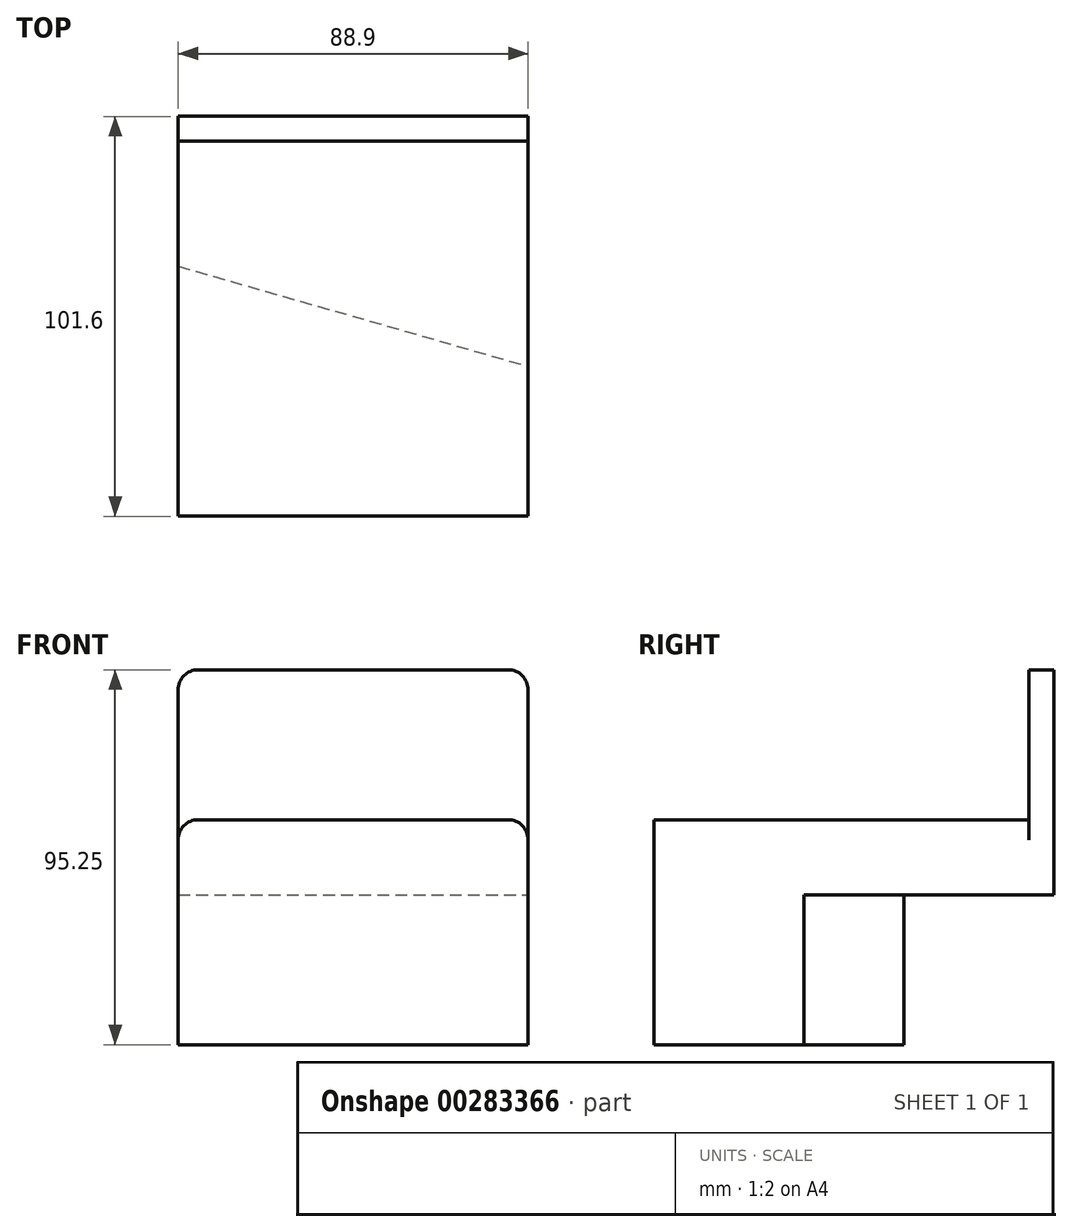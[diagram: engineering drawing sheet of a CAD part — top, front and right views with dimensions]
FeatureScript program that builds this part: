
annotation { "Feature Type Name" : "Feature", "Feature Type Description" : "" }
export const myFeature = defineFeature(function(context is Context, id is Id, definition is map)
    precondition{}
    {
        {
            var Q0;
            Q0=qCreatedBy(makeId("Top.planeOp"),FACE);
            var sketch = newSketch(context, id + "F0", { "sketchPlane" : qUnion([Q0])});
            skLineSegment(sketch, "E0", {"start": v(-31.98, -40.3) * mm, "end": v(56.92, -40.3) * mm});
            skLineSegment(sketch, "E1", {"start": v(56.92, -40.3) * mm, "end": v(56.92, -2.2) * mm});
            skLineSegment(sketch, "E2", {"start": v(-31.98, -40.3) * mm, "end": v(-31.98, 23.2) * mm});
            skLineSegment(sketch, "E3", {"start": v(-31.98, 23.2) * mm, "end": v(56.92, -2.2) * mm});
            skSolve(sketch);
        }
        {
            var Q0;
            Q0 = qSketchRegion(id + "F0", true);
            var Q1;
            Q1 = qSketchRegion(id + "F2", true);
            extrude(context, id + "F1", {"entities" : qUnion([Q0, Q1]), "depth" : 38.1 * mm});
        }
        {
            var Q0;
            Q0=makeQuery(id+"F1.opExtrude","CAP_FACE",FACE,{"disambiguationData":[OSD([sQuery(id+"F0.wireOp",EDGE,"E0"),sQuery(id+"F0.wireOp",EDGE,"E1"),sQuery(id+"F0.wireOp",EDGE,"E2"),sQuery(id+"F0.wireOp",EDGE,"E3")])],"isStart":false});
            var sketch = newSketch(context, id + "F2", { "sketchPlane" : qUnion([Q0])});
            skLineSegment(sketch, "E4.bottom", {"start": v(-31.98, -40.3) * mm, "end": v(56.92, -40.3) * mm});
            skLineSegment(sketch, "E4.top", {"start": v(-31.98, 61.3) * mm, "end": v(56.92, 61.3) * mm});
            skLineSegment(sketch, "E4.left", {"start": v(-31.98, -40.3) * mm, "end": v(-31.98, 61.3) * mm});
            skLineSegment(sketch, "E4.right", {"start": v(56.92, -40.3) * mm, "end": v(56.92, 61.3) * mm});
            skSolve(sketch);
        }
        {
            var Q0;
            Q0 = qSketchRegion(id + "F2", true);
            extrude(context, id + "F3", {"entities" : qUnion([Q0]), "operationType" : NewBodyOperationType.ADD, "depth" : 19.05 * mm});
        }
        {
            var Q0;
            Q0=makeQuery(id+"F3.opExtrude","CAP_FACE",FACE,{"disambiguationData":[OSD([sQuery(id+"F2.wireOp",EDGE,"E4.bottom"),sQuery(id+"F2.wireOp",EDGE,"E4.top"),sQuery(id+"F2.wireOp",EDGE,"E4.left"),sQuery(id+"F2.wireOp",EDGE,"E4.right")])],"isStart":false});
            var sketch = newSketch(context, id + "F4", { "sketchPlane" : qUnion([Q0])});
            skLineSegment(sketch, "E5.bottom", {"start": v(-31.98, 61.3) * mm, "end": v(56.92, 61.3) * mm});
            skLineSegment(sketch, "E5.top", {"start": v(-31.98, 54.95) * mm, "end": v(56.92, 54.95) * mm});
            skLineSegment(sketch, "E5.left", {"start": v(-31.98, 61.3) * mm, "end": v(-31.98, 54.95) * mm});
            skLineSegment(sketch, "E5.right", {"start": v(56.92, 61.3) * mm, "end": v(56.92, 54.95) * mm});
            skSolve(sketch);
        }
        {
            var Q0;
            Q0 = qSketchRegion(id + "F4", true);
            extrude(context, id + "F5", {"entities" : qUnion([Q0]), "operationType" : NewBodyOperationType.ADD, "depth" : 38.1 * mm});
        }
        {
            var Q0;
            Q0=makeQuery(id+"F3.opExtrude","CAP_EDGE",EDGE,{"disambiguationData":[OSD([sQuery(id+"F2.wireOp",EDGE,"E4.right")])],"isStart":false});
            var Q1;
            Q1=makeQuery(id+"F3.opExtrude","CAP_EDGE",EDGE,{"disambiguationData":[OSD([sQuery(id+"F2.wireOp",EDGE,"E4.left")])],"isStart":false});
            var Q2;
            Q2=makeQuery(id+"F5.opExtrude","CAP_EDGE",EDGE,{"disambiguationData":[OSD([sQuery(id+"F4.wireOp",EDGE,"E5.left")])],"isStart":false});
            var Q3;
            Q3=makeQuery(id+"F5.opExtrude","CAP_EDGE",EDGE,{"disambiguationData":[OSD([sQuery(id+"F4.wireOp",EDGE,"E5.right")])],"isStart":false});
            fillet(context, id + "F6", {"entities" : qUnion([Q0, Q1, Q2, Q3]), "radius" : 5.08 * mm, "tangentPropagation" : true, "allowEdgeOverflow" : false});
        }
    });
